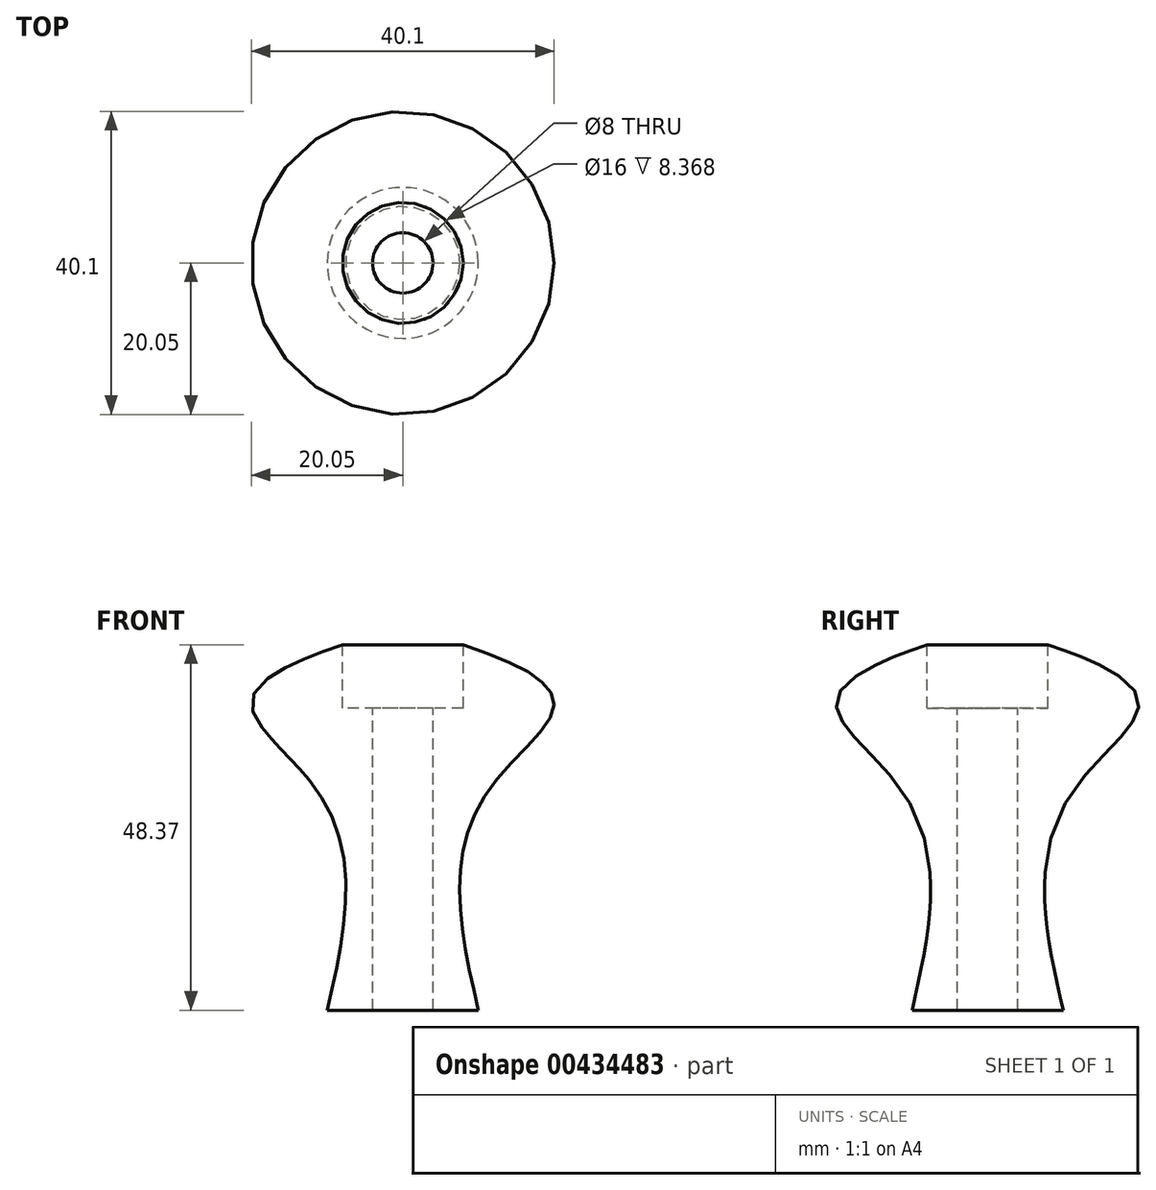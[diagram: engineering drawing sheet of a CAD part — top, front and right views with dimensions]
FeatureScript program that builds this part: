
annotation { "Feature Type Name" : "Feature", "Feature Type Description" : "" }
export const myFeature = defineFeature(function(context is Context, id is Id, definition is map)
    precondition{}
    {
        {
            var Q0;
            Q0=qCreatedBy(makeId("Top.planeOp"),FACE);
            cPlane(context, id + "F0", {"entities" : qUnion([Q0]), "cplaneType" : CPlaneType.OFFSET, "offset" : 30 * mm, "width" : 150 * mm, "height" : 150 * mm});
        }
        {
            var Q0;
            Q0=qCreatedBy(makeId("Top.planeOp"),FACE);
            cPlane(context, id + "F1", {"entities" : qUnion([Q0]), "cplaneType" : CPlaneType.OFFSET, "offset" : 40 * mm, "width" : 150 * mm, "height" : 150 * mm});
        }
        {
            var Q0;
            Q0=qCreatedBy(makeId("Top.planeOp"),FACE);
            cPlane(context, id + "F2", {"entities" : qUnion([Q0]), "cplaneType" : CPlaneType.OFFSET, "offset" : 50 * mm, "width" : 150 * mm, "height" : 150 * mm});
        }
        {
            var Q0;
            Q0=qCreatedBy(makeId("Top.planeOp"),FACE);
            var sketch = newSketch(context, id + "F3", { "sketchPlane" : qUnion([Q0])});
            skCircle(sketch, "E0", {"center": v(0, 0) * mm, "radius": 10 * mm});
            skSolve(sketch);
        }
        {
            var Q0;
            Q0=qCreatedBy(id+"F0.planeOp",FACE);
            var sketch = newSketch(context, id + "F4", { "sketchPlane" : qUnion([Q0])});
            skCircle(sketch, "E1", {"center": v(0, 0) * mm, "radius": 12 * mm});
            skSolve(sketch);
        }
        {
            var Q0;
            Q0=qCreatedBy(id+"F1.planeOp",FACE);
            var sketch = newSketch(context, id + "F5", { "sketchPlane" : qUnion([Q0])});
            skCircle(sketch, "E2", {"center": v(0, 0) * mm, "radius": 20 * mm});
            skSolve(sketch);
        }
        {
            var Q0;
            Q0=qCreatedBy(id+"F2.planeOp",FACE);
            var sketch = newSketch(context, id + "F6", { "sketchPlane" : qUnion([Q0])});
            skCircle(sketch, "E3", {"center": v(0, 0) * mm, "radius": 2.97 * mm});
            skSolve(sketch);
        }
        {
            var Q0;
            Q0=makeQuery(id+"F3.imprint","IMPRINT",FACE,{"disambiguationData":[TD([[makeQuery(id+"F3.imprint","IMPRINT",EDGE,{"derivedFrom":sQuery(id+"F3.wireOp",EDGE,"E0")}),1.0]])]});
            var Q1;
            Q1=makeQuery(id+"F4.imprint","IMPRINT",FACE,{"disambiguationData":[TD([[makeQuery(id+"F4.imprint","IMPRINT",EDGE,{"derivedFrom":sQuery(id+"F4.wireOp",EDGE,"E1")}),1.0]])]});
            var Q2;
            Q2=makeQuery(id+"F5.imprint","IMPRINT",FACE,{"disambiguationData":[TD([[makeQuery(id+"F5.imprint","IMPRINT",EDGE,{"derivedFrom":sQuery(id+"F5.wireOp",EDGE,"E2")}),1.0]])]});
            var Q3;
            Q3=makeQuery(id+"F6.imprint","IMPRINT",FACE,{"disambiguationData":[TD([[makeQuery(id+"F6.imprint","IMPRINT",EDGE,{"derivedFrom":sQuery(id+"F6.wireOp",EDGE,"E3")}),1.0]])]});
            loft(context, id + "F7", {"sheetProfilesArray" : [{ "sheetProfileEntities" : qUnion([Q0]) }, { "sheetProfileEntities" : qUnion([Q1]) }, { "sheetProfileEntities" : qUnion([Q2]) }, { "sheetProfileEntities" : qUnion([Q3]) }]});
        }
        {
            var Q0;
            Q0=qCreatedBy(id+"F2.planeOp",FACE);
            var sketch = newSketch(context, id + "F8", { "sketchPlane" : qUnion([Q0])});
            skCircle(sketch, "E4", {"center": v(0, 0) * mm, "radius": 4 * mm});
            skSolve(sketch);
        }
        {
            var Q0;
            Q0 = qSketchRegion(id + "F8", true);
            extrude(context, id + "F9", {"entities" : qUnion([Q0]), "operationType" : NewBodyOperationType.REMOVE, "oppositeDirection" : true, "depth" : 91 * mm});
        }
        {
            var Q0;
            Q0=qCreatedBy(id+"F2.planeOp",FACE);
            var sketch = newSketch(context, id + "F10", { "sketchPlane" : qUnion([Q0])});
            skCircle(sketch, "E5", {"center": v(0, 0) * mm, "radius": 8 * mm});
            skSolve(sketch);
        }
        {
            var Q0;
            Q0=makeQuery(id+"F10.imprint","IMPRINT",FACE,{"disambiguationData":[TD([[makeQuery(id+"F10.imprint","IMPRINT",EDGE,{"derivedFrom":sQuery(id+"F10.wireOp",EDGE,"E5")}),1.0]])]});
            extrude(context, id + "F11", {"entities" : qUnion([Q0]), "operationType" : NewBodyOperationType.REMOVE, "oppositeDirection" : true, "depth" : 10 * mm});
        }
    });
